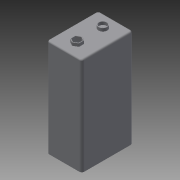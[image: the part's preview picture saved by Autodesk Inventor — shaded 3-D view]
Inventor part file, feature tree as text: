
AUTODESK INVENTOR PART (.ipt)
format: ipt  version: 2015 (Build 190159000, 159)  size: 182,784 bytes
history: native  units: in
note: dims shown in document units (in); Inventor stores cm internally (conversion verified against a paired STEP export)
features: fillet x5, extrude x3, sketch x3, shell x2
ambient origin geometry x8: Origin, YZ Plane, XZ Plane, XY Plane, X Axis, Y Axis, Z Axis, Center Point
bodies: Solid1 (feature_tree)
feature tree (13):
  extrude  "Extrusion1"  Depth=1.0in
  extrude  "Extrusion2"  Depth=1.9in TaperAngle=0.0deg
  shell  "Shell1"  Thickness=0.1in
  extrude  "Extrusion3"  Depth=0.03in
  shell  "Shell2"  Thickness=0.25in
  fillet  "Fillet1"  Radius=0.06in
  fillet  "Fillet2"  Radius=0.015in
  fillet  "Fillet3"  Radius=0.173in
  fillet  "Fillet4"  Radius=0.34in
  fillet  "Fillet5"  Radius=0.25in
  sketch  "Sketch1"  dims[d0=0.68in d1=1.0in]
  sketch  "Sketch2"  dims[d2=0.05in d3=1.9in d4=0.0in d5=0.1in]
  sketch  "Sketch3"  dims[d6=0.68in d7=0.34in d8=0.25in d9=0.06in d10=0.0in d11=0.015in d12=0.173in d13=0.34in d14=0.25in d15=0.06in d16=0.0in d17=0.015in d18=0.01in d19=0.005in d20=0.005in d21=0.005in d22=0.03in]
